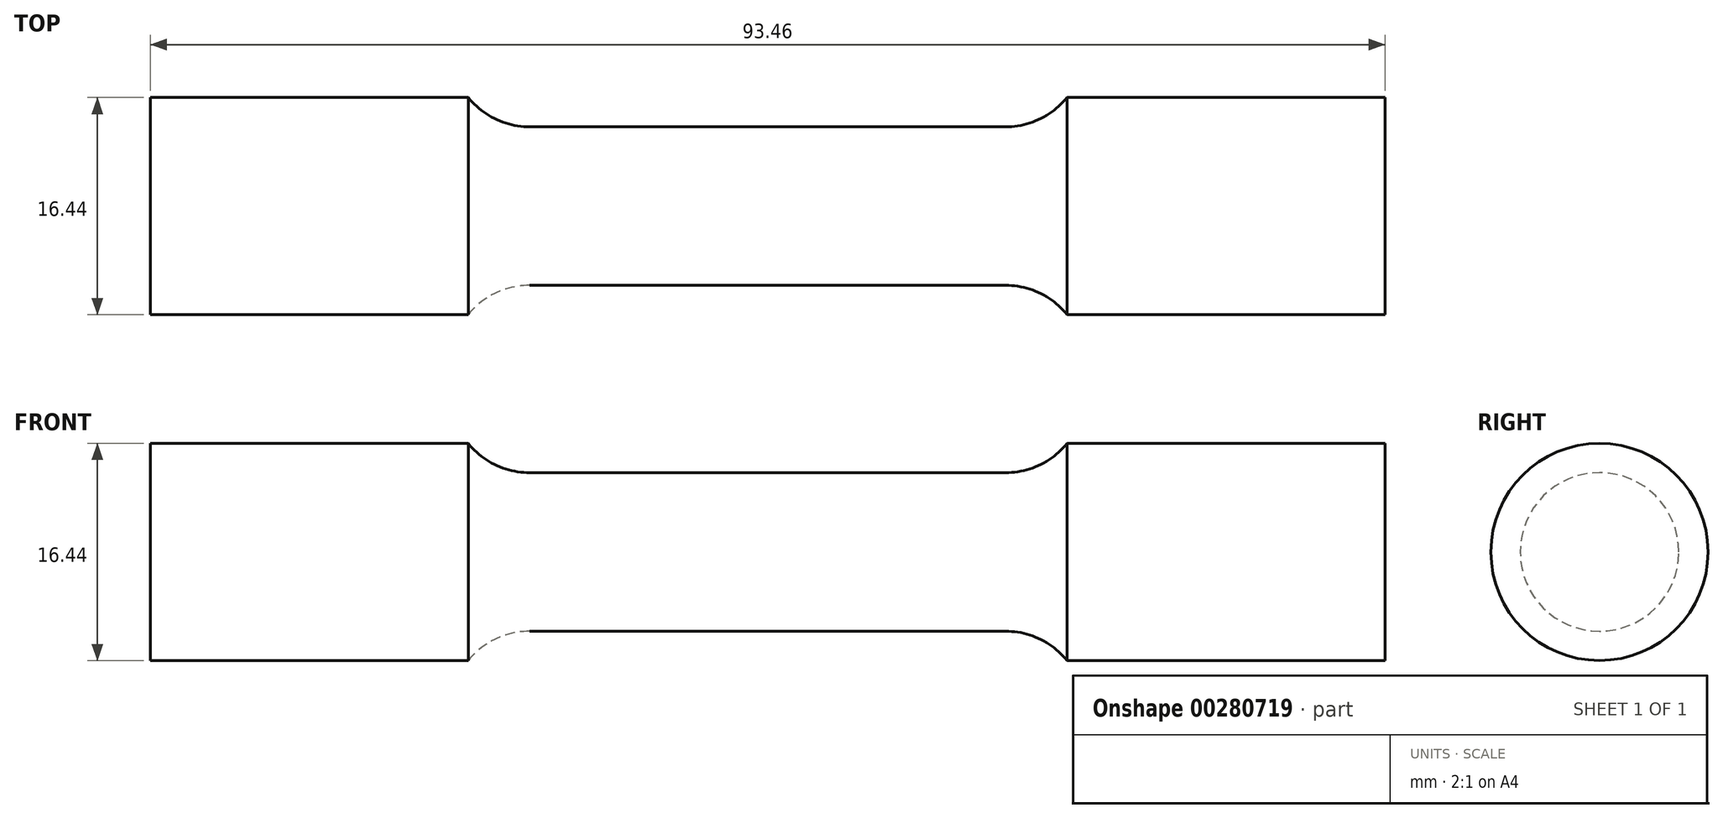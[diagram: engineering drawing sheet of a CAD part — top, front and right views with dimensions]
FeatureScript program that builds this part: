
annotation { "Feature Type Name" : "Feature", "Feature Type Description" : "" }
export const myFeature = defineFeature(function(context is Context, id is Id, definition is map)
    precondition{}
    {
        {
            var Q0;
            Q0=qCreatedBy(makeId("Front.planeOp"),FACE);
            var sketch = newSketch(context, id + "F0", { "sketchPlane" : qUnion([Q0])});
            skLineSegment(sketch, "E0", {"start": v(0, 6) * mm, "end": v(18, 6) * mm});
            skArc(sketch, "E1", {"start": v(18, 6) * mm, "mid": v(20.58, 6.58) * mm, "end": v(22.66, 8.22) * mm});
            skLineSegment(sketch, "E2", {"start": v(22.66, 8.22) * mm, "end": v(46.73, 8.22) * mm});
            skLineSegment(sketch, "E3", {"start": v(46.73, 8.22) * mm, "end": v(46.73, 0) * mm});
            skLineSegment(sketch, "E4.MirrorCS", {"start": v(0, 6) * mm, "end": v(-18, 6) * mm});
            skLineSegment(sketch, "E5.MirrorCS", {"start": v(-46.73, 8.22) * mm, "end": v(-46.73, 0) * mm});
            skLineSegment(sketch, "E6.MirrorCS", {"start": v(-22.66, 8.22) * mm, "end": v(-46.73, 8.22) * mm});
            skArc(sketch, "E7.MirrorCS", {"start": v(-18, 6) * mm, "mid": v(-20.58, 6.58) * mm, "end": v(-22.66, 8.22) * mm});
            skLineSegment(sketch, "E8", {"start": v(-46.73, 0) * mm, "end": v(46.73, 0) * mm});
            skSolve(sketch);
        }
        {
            var Q0;
            Q0 = qSketchRegion(id + "F0", true);
            var Q1;
            Q1=sQuery(id+"F0.wireOp",EDGE,"E8");
            revolve(context, id + "F1", {"entities" : qUnion([Q0]), "axis" : qUnion([Q1]), "revolveType" : RevolveType.FULL});
        }
    });
